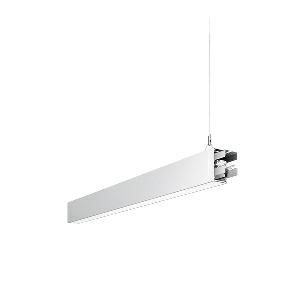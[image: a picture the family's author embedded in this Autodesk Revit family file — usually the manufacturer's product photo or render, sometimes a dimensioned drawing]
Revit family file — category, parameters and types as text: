
# Revit family: idoo_line_-_ilp_2000_830_d_mid_00805711_98e9
name_source: partatom
category: Lighting Fixtures
units: mm (PartAtom-declared; Revit-internal decimal feet)

## family parameters
Cut with Voids When Loaded = No
Host = Face
Light Source = No
Part Type = Normal
Room Calculation Point = No
Round Connector Dimension = Use Diameter
Shared = No

## types (1)
- IDOO.line - ILP 2000/830/D MID (1 x LED, 2250 lm, 3000K)
    Apparent Load = 17 VA
    Approval mark = CE
    CIE Flux Codes = 66 91 98 40 100
    Color Rendering = 80-89
    Color Temperature = 3000K
    Control Gear = Electronic ballast
    Default Elevation = 1800 mm
    Description = ILP 2000/830/D|Suspended luminaire|light source: LED|connected load: 220-240 V, 50/60 Hz|Power consumption: approx. 17 W|standby: approx. 0,20|luminous flux: 2250 lm|luminous efficacy: 132 lm/W|light distribution: Direct/indirect|direct ratio: approx. 40 %|colour temperature: Warm white, ca. 3000 K|color rendering index (CRI): >= 80|chromaticity tolerance:  3 SDCM|System of protection: IP 40|technology: Continuously dimmable|luminaire body|material: Sectional aluminium|colour: White|lamp cover: Acrylic (PMMA), Clear|mains lead: 1,0 m With free stranded wires|Fastening: Steel cable 0.3 - 0.7 m|glare control: Prism aperture|luminance(L65): <= 2700 cd/m|unified glare rating(4H 8H): <=  16|special features: DALI Load 1x, TouchDIM - dimming via standard switch, Through-wired, up to 18 m on one mains connection, Flicker-free, Suitable as emergency lighting, Mechanical and electrical connection of the individual modules without tools|
    Frequency = 50 Hz
    Height = 110 mm
    Lamp = 1 x LED
    Lamp Light Flux = 2250 lm
    Lamp count = 1
    Length = 842 mm
    Luminous efficacy = 132 lm/W
    Manufacturer = Waldmann
    ModVariant = No
    Model = 00805711
    Mounting Place = Ceiling
    Mounting Type = Pendant
    Number of Poles = 1
    OnlyDefault = Yes
    Power Factor = 1
    Product Name = IDOO.line - ILP 2000/830/D MID
    Product group = Suspended luminaire
    ProductGroupID = 9
    Protection Class = Protection class I
    Protection Degree = IP 40
    RLX_Detail_Level = 1
    RLX_Emergency_Light_Flux = 0 lm
    RLX_Emergency_Type = 0
    RLX_Emergency_Type_DB = No
    RlxData = <blob elided: 17893 chars, md5=1d84a6b1>
    Socket = socket
    Standby Power = 0 W
    System Light Flux = 2250 lm
    System Power = 17 W
    Type Comments = Product without accessories
    Type Image = 113296000-00692546.jpg
    URL = http://relux.com
    VarID = ---
    Voltage = 230 V
    Voltage Range = 220-240 V
    Weight = 0.00 kg
    Width = 60 mm  [stored 0.19685 ft]

note: [stored X ft] marks values corroborated as IEEE doubles in the binary element streams (Revit-internal decimal feet)

## geometry (parser evidence)
native form markers: Blend x4, Sweep x14
no freeform markers — native parametric forms only
